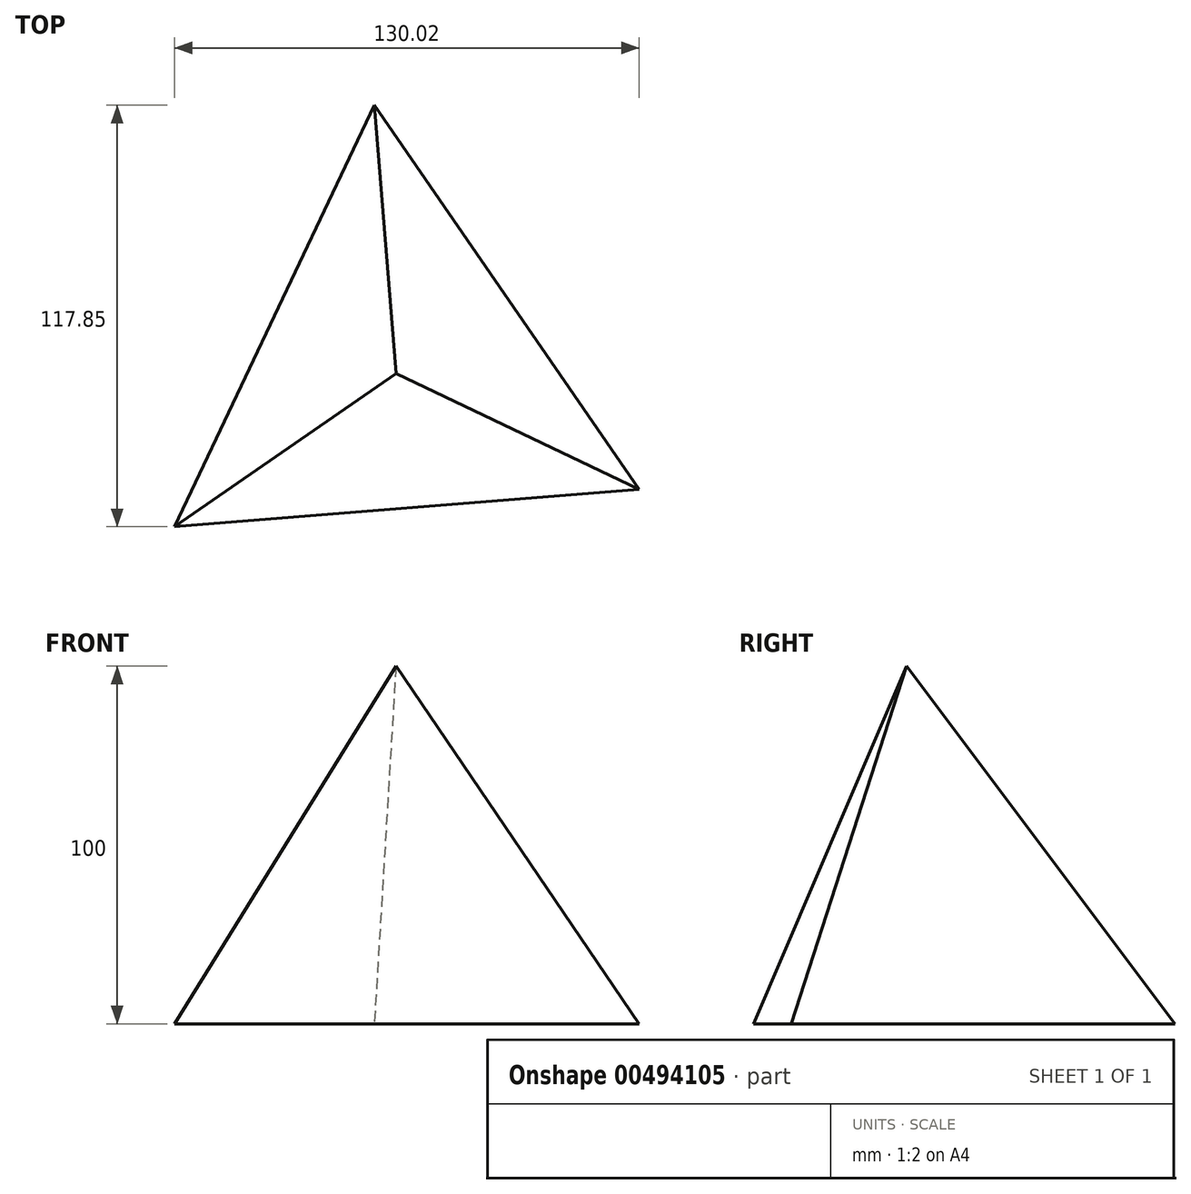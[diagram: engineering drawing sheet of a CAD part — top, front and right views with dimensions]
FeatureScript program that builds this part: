
annotation { "Feature Type Name" : "Feature", "Feature Type Description" : "" }
export const myFeature = defineFeature(function(context is Context, id is Id, definition is map)
    precondition{}
    {
        {
            var Q0;
            Q0=qCreatedBy(makeId("Top.planeOp"),FACE);
            var sketch = newSketch(context, id + "F0", { "sketchPlane" : qUnion([Q0])});
            skCircle(sketch, "E0.cCircle", {"center": v(0, 0) * mm, "radius": 75.31 * mm, "construction": true});
            skLineSegment(sketch, "E0.0", {"start": v(-6.06, 75.07) * mm, "end": v(68.04, -32.29) * mm});
            skLineSegment(sketch, "E0.1", {"start": v(68.04, -32.29) * mm, "end": v(-61.98, -42.78) * mm});
            skLineSegment(sketch, "E0.2", {"start": v(-61.98, -42.78) * mm, "end": v(-6.06, 75.07) * mm});
            skSolve(sketch);
        }
        {
            var Q0;
            Q0=qCreatedBy(makeId("Top.planeOp"),FACE);
            cPlane(context, id + "F1", {"entities" : qUnion([Q0]), "cplaneType" : CPlaneType.OFFSET, "offset" : 100 * mm, "width" : 150 * mm, "height" : 150 * mm});
        }
        {
            var Q0;
            Q0=qCreatedBy(id+"F1.planeOp",FACE);
            var sketch = newSketch(context, id + "F2", { "sketchPlane" : qUnion([Q0])});
            skPoint(sketch, "E1", {"position": v(-3.73, 2.73) * mm});
            skPoint(sketch, "E2", {"position": v(0, 0) * mm});
            skSolve(sketch);
        }
        {
            var Q0;
            Q0=sQuery(id+"F2.wireOp",VERTEX,"E2");
            var Q1;
            Q1=makeQuery(id+"F0.imprint","IMPRINT",FACE,{"disambiguationData":[TD([[makeQuery(id+"F0.imprint","IMPRINT",EDGE,{"derivedFrom":sQuery(id+"F0.wireOp",EDGE,"E0.0")}),-1.0]])]});
            loft(context, id + "F3", {"sheetProfilesArray" : [{ "sheetProfileEntities" : qUnion([Q0]) }, { "sheetProfileEntities" : qUnion([Q1]) }]});
        }
    });
